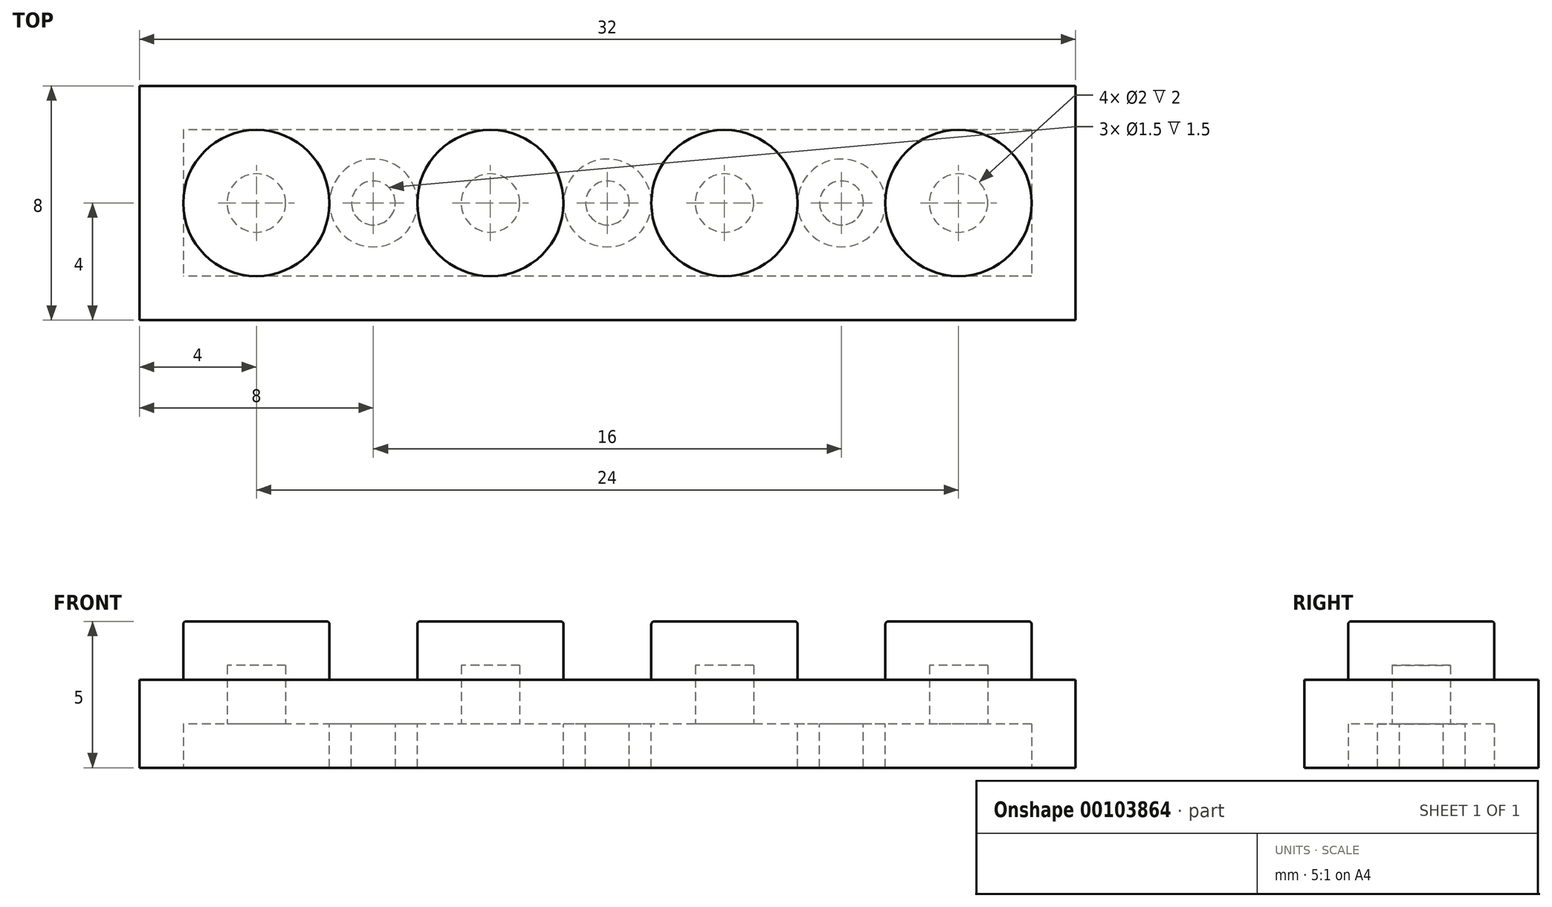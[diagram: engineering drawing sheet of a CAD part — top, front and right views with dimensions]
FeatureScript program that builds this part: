
annotation { "Feature Type Name" : "Feature", "Feature Type Description" : "" }
export const myFeature = defineFeature(function(context is Context, id is Id, definition is map)
    precondition{}
    {
        {
            var Q0;
            Q0=qCreatedBy(makeId("Top.planeOp"),FACE);
            var sketch = newSketch(context, id + "F0", { "sketchPlane" : qUnion([Q0])});
            skLineSegment(sketch, "E0.bottom", {"start": v(16, 4) * mm, "end": v(-16, 4) * mm});
            skLineSegment(sketch, "E0.top", {"start": v(16, -4) * mm, "end": v(-16, -4) * mm});
            skLineSegment(sketch, "E0.left", {"start": v(16, 4) * mm, "end": v(16, -4) * mm});
            skLineSegment(sketch, "E0.right", {"start": v(-16, 4) * mm, "end": v(-16, -4) * mm});
            skPoint(sketch, "E0.middle", {"position": v(0, 0) * mm});
            skSolve(sketch);
        }
        {
            var Q0;
            Q0=makeQuery(id+"F0.imprint","IMPRINT",FACE,{"disambiguationData":[TD([[makeQuery(id+"F0.imprint","IMPRINT",EDGE,{"derivedFrom":sQuery(id+"F0.wireOp",EDGE,"E0.bottom")}),1.0]])]});
            extrude(context, id + "F1", {"entities" : qUnion([Q0]), "depth" : 3 * mm});
        }
        {
            var Q0;
            Q0=makeQuery(id+"F1.opExtrude","CAP_FACE",FACE,{"disambiguationData":[OSD([sQuery(id+"F0.wireOp",EDGE,"E0.bottom"),sQuery(id+"F0.wireOp",EDGE,"E0.top"),sQuery(id+"F0.wireOp",EDGE,"E0.left"),sQuery(id+"F0.wireOp",EDGE,"E0.right")])],"isStart":false});
            var sketch = newSketch(context, id + "F2", { "sketchPlane" : qUnion([Q0])});
            skCircle(sketch, "E1", {"center": v(-12, 0) * mm, "radius": 2.5 * mm});
            skCircle(sketch, "E2.1.0.0", {"center": v(-4, 0) * mm, "radius": 2.5 * mm});
            skCircle(sketch, "E2.2.0.0", {"center": v(4, 0) * mm, "radius": 2.5 * mm});
            skCircle(sketch, "E2.3.0.0", {"center": v(12, 0) * mm, "radius": 2.5 * mm});
            skLineSegment(sketch, "E2.direction1", {"start": v(-12, 0) * mm, "end": v(-4, 0) * mm, "construction": true});
            skLineSegment(sketch, "E3", {"start": v(-4, 0) * mm, "end": v(4, 0) * mm, "construction": true});
            skSolve(sketch);
        }
        {
            var Q0;
            Q0 = qSketchRegion(id + "F2", true);
            extrude(context, id + "F3", {"entities" : qUnion([Q0]), "operationType" : NewBodyOperationType.ADD, "depth" : 2 * mm});
        }
        {
            var Q0;
            Q0=makeQuery(id+"F3.opExtrude","CAP_EDGE",EDGE,{"disambiguationData":[OSD([sQuery(id+"F2.wireOp",EDGE,"E1")])],"isStart":false});
            var Q1;
            Q1=makeQuery(id+"F3.opExtrude","CAP_EDGE",EDGE,{"disambiguationData":[OSD([sQuery(id+"F2.wireOp",EDGE,"E2.1.0.0")])],"isStart":false});
            var Q2;
            Q2=makeQuery(id+"F3.opExtrude","CAP_EDGE",EDGE,{"disambiguationData":[OSD([sQuery(id+"F2.wireOp",EDGE,"E2.2.0.0")])],"isStart":false});
            var Q3;
            Q3=makeQuery(id+"F3.opExtrude","CAP_EDGE",EDGE,{"disambiguationData":[OSD([sQuery(id+"F2.wireOp",EDGE,"E2.3.0.0")])],"isStart":false});
            fillet(context, id + "F4", {"entities" : qUnion([Q0, Q1, Q2, Q3]), "radius" : 0.1 * mm, "tangentPropagation" : true, "allowEdgeOverflow" : false});
        }
        {
            var Q0;
            Q0=makeQuery(id+"F1.opExtrude","CAP_FACE",FACE,{"disambiguationData":[OSD([sQuery(id+"F0.wireOp",EDGE,"365ffcde-021b-4e51-809e-17f9b7e04258.bottom"),sQuery(id+"F0.wireOp",EDGE,"365ffcde-021b-4e51-809e-17f9b7e04258.top"),sQuery(id+"F0.wireOp",EDGE,"365ffcde-021b-4e51-809e-17f9b7e04258.left"),sQuery(id+"F0.wireOp",EDGE,"365ffcde-021b-4e51-809e-17f9b7e04258.right")])],"isStart":true});
            var Q1;
            Q1=makeQuery(id+"F1.opExtrude","CAP_FACE",FACE,{"disambiguationData":[OSD([sQuery(id+"F0.wireOp",EDGE,"E0.bottom"),sQuery(id+"F0.wireOp",EDGE,"E0.top"),sQuery(id+"F0.wireOp",EDGE,"E0.left"),sQuery(id+"F0.wireOp",EDGE,"E0.right")])],"isStart":true});
            shell(context, id + "F5", {"entities" : qUnion([Q0, Q1]), "thickness" : 1.5 * mm});
        }
        {
            var Q0;
            Q0=makeQuery(id+"F5.opShell","OFFSET_FACE",FACE,{"disambiguationData":[OSD([sQuery(id+"F0.wireOp",EDGE,"E0.bottom"),sQuery(id+"F0.wireOp",EDGE,"E0.top"),sQuery(id+"F0.wireOp",EDGE,"E0.left"),sQuery(id+"F0.wireOp",EDGE,"E0.right")])]});
            var sketch = newSketch(context, id + "F6", { "sketchPlane" : qUnion([Q0])});
            skLineSegment(sketch, "E4", {"start": v(0, 2.5) * mm, "end": v(0, -2.5) * mm, "construction": true});
            skCircle(sketch, "E5", {"center": v(-8, 0) * mm, "radius": 1.5 * mm});
            skCircle(sketch, "E6.0", {"center": v(-8, 0) * mm, "radius": 0.75 * mm});
            skLineSegment(sketch, "E7.0", {"start": v(19.5, -7.5) * mm, "end": v(19.5, 7.5) * mm});
            skLineSegment(sketch, "E7.1", {"start": v(-19.5, -7.5) * mm, "end": v(19.5, -7.5) * mm});
            skLineSegment(sketch, "E7.2", {"start": v(-19.5, 7.5) * mm, "end": v(-19.5, -7.5) * mm});
            skLineSegment(sketch, "E7.3", {"start": v(19.5, 7.5) * mm, "end": v(-19.5, 7.5) * mm});
            skCircle(sketch, "E8.1.0.0", {"center": v(0, 0) * mm, "radius": 1.5 * mm});
            skCircle(sketch, "E8.1.0.1", {"center": v(0, 0) * mm, "radius": 0.75 * mm});
            skCircle(sketch, "E8.2.0.0", {"center": v(8, 0) * mm, "radius": 1.5 * mm});
            skCircle(sketch, "E8.2.0.1", {"center": v(8, 0) * mm, "radius": 0.75 * mm});
            skLineSegment(sketch, "E8.direction1", {"start": v(-8, 0) * mm, "end": v(0, 0) * mm, "construction": true});
            skSolve(sketch);
        }
        {
            var Q0;
            Q0=makeQuery(id+"F6.imprint","IMPRINT",FACE,{"disambiguationData":[TD([[makeQuery(id+"F6.imprint","IMPRINT",EDGE,{"derivedFrom":sQuery(id+"F6.wireOp",EDGE,"E5")}),1.0]])]});
            var Q1;
            Q1=makeQuery(id+"F6.imprint","IMPRINT",FACE,{"disambiguationData":[TD([[makeQuery(id+"F6.imprint","IMPRINT",EDGE,{"derivedFrom":sQuery(id+"F6.wireOp",EDGE,"E8.1.0.0")}),1.0]])]});
            var Q2;
            Q2=makeQuery(id+"F6.imprint","IMPRINT",FACE,{"disambiguationData":[TD([[makeQuery(id+"F6.imprint","IMPRINT",EDGE,{"derivedFrom":sQuery(id+"F6.wireOp",EDGE,"E8.2.0.0")}),1.0]])]});
            var Q3;
            Q3=makeQuery(id+"F1.opExtrude","CAP_FACE",FACE,{"disambiguationData":[OSD([sQuery(id+"F0.wireOp",EDGE,"E0.bottom"),sQuery(id+"F0.wireOp",EDGE,"E0.top"),sQuery(id+"F0.wireOp",EDGE,"E0.left"),sQuery(id+"F0.wireOp",EDGE,"E0.right")])],"isStart":true});
            extrude(context, id + "F7", {"entities" : qUnion([Q0, Q1, Q2]), "operationType" : NewBodyOperationType.ADD, "endBound" : BoundingType.UP_TO_SURFACE, "endBoundEntityFace" : qUnion([Q3]), "depth" : 25 * mm});
        }
    });
